# Revit family: CLR-01_RFA
name_source: partatom
category: Aparatos sanitarios
units: mm (PartAtom-declared; Revit-internal decimal feet)

## family parameters
Activar corte en vistas = No
Compartido = Sí
Corte con vacíos al cargar = No
Cota de conector redondo = Usar diámetro
Mantener orientación de anotación = No
Número OmniClass = 23.45.05.14.99
Punto de cálculo de habitación = Sí
Se basa en plano de trabajo = No
Siempre vertical = Sí
Tipo de pieza = Normal
Título OmniClass = Other Sanitary Washing Plumbing Fixtures

## types (1)
- CLR-01
    Brass Chromed = Brass
    Comentarios de tipo = Contra
    Descripción = Contra con rejilla para lavabo con rebosadero.
Acabado: Cromo.
    Elevación por Defecto = 1"
    Elevación por defecto = 0"
    Fabricante = HELVEX
    Features = Contra
    Imagen de tipo = CLR-01.png
    Inlet Threads = 1 ¼" Pipe
    Modelo = CLR-01
    Total Diameter = 2"
    Total Height = 6"
    URL = https://proyecta.helvex.com

## geometry (parser evidence)
native form markers: Sweep x3
no freeform markers — native parametric forms only
